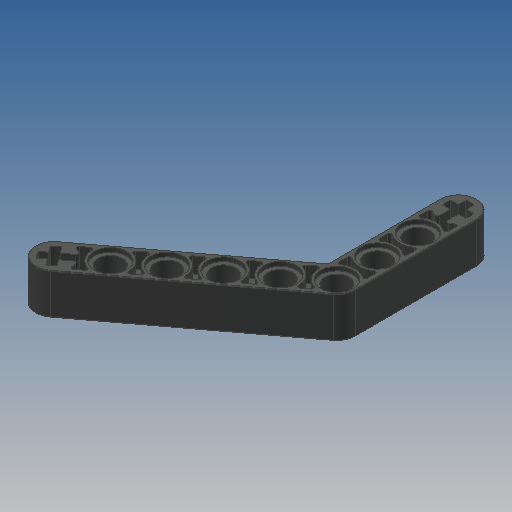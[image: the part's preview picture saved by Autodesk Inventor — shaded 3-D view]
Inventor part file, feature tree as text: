
AUTODESK INVENTOR PART (.ipt)
format: ipt  version: 2022.2 (Build 262287010, 287A)  size: 443,904 bytes
history: native  units: mm
features: extrude x3, sketch x1, mirror x1, fillet x1, projected_geometry x1
ambient origin geometry x8: Origin, YZ Plane, XZ Plane, XY Plane, X Axis, Y Axis, Z Axis, Center Point
bodies: Solid1 (feature_tree)
feature tree (7):
  extrude  "Extrusion1"  Depth=7.2mm
  sketch  "Sketch6"  dims[d14=8.0mm d15=0.0mm d32=7.2mm d41=0.8mm d42=0.0mm d43=3.1mm d44=0.0mm d49=6.4mm d50=4.8mm d52=0.8mm d60=0.4mm d61=0.1mm d62=1.6mm d76=8.0mm d77=8.0mm d78=4.8mm d79=30.0mm d81=8.0mm d82=10.0mm d84=10.0mm d86=0.8mm d87=50.0mm d89=8.0mm d90=10.0mm d92=10.0mm d94=1.6mm d95=1.6mm d96=1.6mm d97=9.272934mm]
  extrude  "Extrusion7"  Depth=0.8mm TaperAngle=0.0deg
  extrude  "Extrusion8"  Depth=3.1mm TaperAngle=0.0deg
  mirror  "Mirror1"
  fillet  "Fillet2"  Radius=6.4mm
  projected_geometry  "Projected Loop5"
